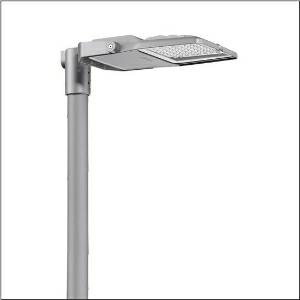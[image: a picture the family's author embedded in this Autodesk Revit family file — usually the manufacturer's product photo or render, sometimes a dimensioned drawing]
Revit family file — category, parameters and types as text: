
# Revit family: floodlight_fl_21_iq_mini___pl33t_5xa7772d4f3a_7ca2
name_source: partatom
category: Lighting Fixtures
units: mm (PartAtom-declared; Revit-internal decimal feet)

## family parameters
Cut with Voids When Loaded = No
Host = Face
Light Source = No
Part Type = Normal
Room Calculation Point = No
Round Connector Dimension = Use Diameter
Shared = No

## types (1)
- --- (1 x LED, 18390 lm, 143 W, 4000K)
    Apparent Load = 143 VA
    CIE Flux Codes = 26 75 99 100 100
    Color Rendering = 70
    Color Temperature = 4000K
    Default Elevation = 1800 mm
    Description = Floodlight FL 21 iQ mini, floodlight, primary light control with lens, of PMMA, primary optical cover: protective disc, of toughened safety glass, transparent, light distribution: PL33T, light emission: direct distribution, installation type: surface-mounted, LED, High Power LED, rated luminous flux: 18.390lm, luminous efficacy: 129lm/W, light colour: 740, colour temperature: 4000K, control gear: iQ Street-Remote/DALI, control: Auto-Match, Temp-Guard, Night-Set, Smart-Wire, Desk-Remote (wireless, voltage-free reading and setting of iQ features in the workshop via application-optimized NFC function/RFID function), optimised constant luminous flux control (CLO 2.0), Light-Fading, Lumen-Switch, with terminal, 6-pole, mains connection: 220..240V, AC, 50/60Hz, start of lifetime: 143W, end of service life: 152W, reduction: 61W, luminaire housing, of diecast aluminium, powder-coated, Siteco® metallic grey (DB 702S), corrosivity category C5 mid according to DIN EN ISO 12944, suitable for swimming pools, chlorine-resistant, sealing non-destructively replaceable, please order mast flange separately, mast bracket, of steel, galvanised, powder-coated, protection rating (complete): IP66, insulation class (complete): insulation class II (safety insulation), certification: CE, ENEC, VDE, protection symbol: D, impact resistance: IK08, permissible operating ambient temperature: -40..+40°C, permissible operating ambient temperature for outdoor applications: -40..+50°C, standard: DIN EN 12944, LABS conformity tested according to VDMA 24364:2018-05, packaging unit: 1 piece

Light Distribution: PL33T
    Height = 70 mm
    Lamp = 1 x LED
    Lamp Light Flux = 18390 lm
    Lamp Power = 143 W
    Lamp count = 1
    Length = 485 mm
    Luminous efficacy = 129 lm/W
    Manufacturer = Siteco
    ModVariant = No
    Model = 5XA7772D4F3A
    Number of Poles = 1
    OnlyDefault = Yes
    Power Factor = 1
    Product Name = Floodlight FL 21 iQ mini | PL33T
    Product group = floodlight | pylon annexe
    ProductGroupID = 6201
    Protection Class = Protection class II
    Protection Degree = IP 66
    RLX_Detail_Level = 1
    RLX_Emergency_Light_Flux = 0 lm
    RLX_Emergency_Type = 0
    RLX_Emergency_Type_DB = No
    RlxData = <blob elided: 101489 chars, md5=c7a89117>
    Socket = socket
    Standby Power = 0 W
    System Light Flux = 18390 lm
    System Power = 143 W
    Type Comments = factory setting: luminous flux: 100 % | dim-lin: 254 | 730 mA
    Type Image = l_1007125.jpg
    URL = http://relux.com
    VarID = @adj_170221
    Voltage = 0 V
    Weight = 0.00 kg
    Width = 337 mm

## geometry (parser evidence)
native form markers: Blend x4, Sweep x12
no freeform markers — native parametric forms only
